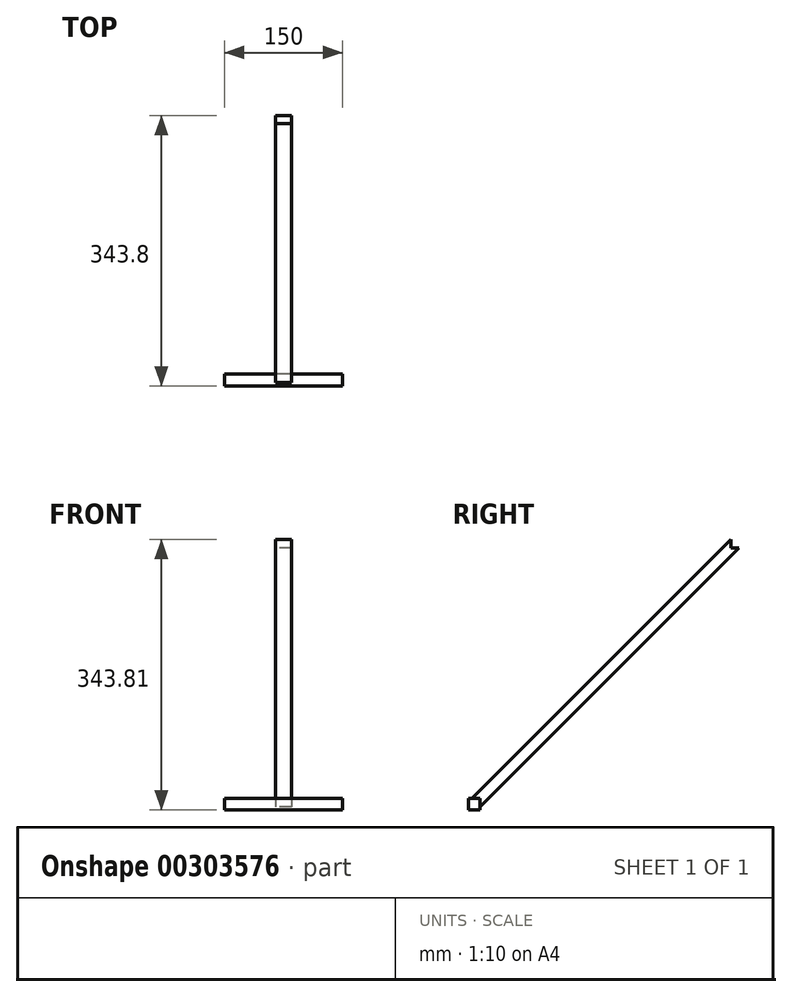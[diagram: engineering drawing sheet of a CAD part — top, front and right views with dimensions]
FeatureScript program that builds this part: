
annotation { "Feature Type Name" : "Feature", "Feature Type Description" : "" }
export const myFeature = defineFeature(function(context is Context, id is Id, definition is map)
    precondition{}
    {
        {
            var Q0;
            Q0=qCreatedBy(makeId("Right.planeOp"),FACE);
            var sketch = newSketch(context, id + "F0", { "sketchPlane" : qUnion([Q0])});
            skLineSegment(sketch, "E0", {"start": v(-179.3, -100.95) * mm, "end": v(149.5, 227.86) * mm});
            skLineSegment(sketch, "E1", {"start": v(160.1, 217.25) * mm, "end": v(-168.7, -111.55) * mm});
            skLineSegment(sketch, "E2", {"start": v(-168.7, -111.55) * mm, "end": v(-179.3, -100.95) * mm});
            skLineSegment(sketch, "E3", {"start": v(13.12, 43.85) * mm, "end": v(-59.7, -28.97) * mm, "construction": true});
            skLineSegment(sketch, "E4.bottom", {"start": v(160.1, 217.25) * mm, "end": v(149.5, 217.25) * mm});
            skLineSegment(sketch, "E4.right", {"start": v(149.5, 217.25) * mm, "end": v(149.5, 227.86) * mm});
            skPoint(sketch, "E4.middle", {"position": v(157.73, 225.48) * mm});
            skLineSegment(sketch, "E5.bottom", {"start": v(-183.7, -100.95) * mm, "end": v(-168.7, -100.95) * mm});
            skLineSegment(sketch, "E5.top", {"start": v(-183.7, -115.95) * mm, "end": v(-168.7, -115.95) * mm});
            skLineSegment(sketch, "E5.left", {"start": v(-183.7, -100.95) * mm, "end": v(-183.7, -115.95) * mm});
            skLineSegment(sketch, "E5.right", {"start": v(-168.7, -100.95) * mm, "end": v(-168.7, -115.95) * mm});
            skPoint(sketch, "E5.middle", {"position": v(-176.2, -108.45) * mm});
            skLineSegment(sketch, "E6", {"start": v(149.5, 227.86) * mm, "end": v(149.5, 217.25) * mm, "construction": true});
            skLineSegment(sketch, "E7", {"start": v(160.1, 217.25) * mm, "end": v(149.5, 217.25) * mm, "construction": true});
            skPoint(sketch, "E4.top.end.orphan", {"position": v(149.5, 233.72) * mm});
            skPoint(sketch, "E4.left.end.orphan", {"position": v(165.96, 233.72) * mm});
            skPoint(sketch, "E8.orphan", {"position": v(165.96, 217.25) * mm});
            skLineSegment(sketch, "E9.bottom", {"start": v(-179.3, -100.95) * mm, "end": v(-168.7, -100.95) * mm, "construction": true});
            skLineSegment(sketch, "E9.top", {"start": v(-179.3, -111.55) * mm, "end": v(-168.7, -111.55) * mm, "construction": true});
            skLineSegment(sketch, "E9.left", {"start": v(-179.3, -100.95) * mm, "end": v(-179.3, -111.55) * mm, "construction": true});
            skLineSegment(sketch, "E9.right", {"start": v(-168.7, -100.95) * mm, "end": v(-168.7, -111.55) * mm, "construction": true});
            skLineSegment(sketch, "E10", {"start": v(149.5, 227.86) * mm, "end": v(160.1, 227.86) * mm, "construction": true});
            skLineSegment(sketch, "E11", {"start": v(160.1, 217.25) * mm, "end": v(160.1, 227.86) * mm, "construction": true});
            skLineSegment(sketch, "E12", {"start": v(149.5, 233.72) * mm, "end": v(165.96, 233.72) * mm, "construction": true});
            skSolve(sketch);
        }
        {
            var Q0;
            {var subQ1=sQuery(id+"F0.wireOp",EDGE,"E0");Q0=makeQuery(id+"F0.imprint","IMPRINT",FACE,{"disambiguationData":[TD([[makeQuery(id+"F0.imprint","IMPRINT",EDGE,{"derivedFrom":subQ1}),-1.0]])]});}
            extrude(context, id + "F1", {"entities" : qUnion([Q0]), "endBound" : BoundingType.SYMMETRIC, "depth" : 20 * mm});
        }
        {
            var Q0;
            {var subQ2=sQuery(id+"F0.wireOp",EDGE,"E2");Q0=makeQuery(id+"F0.imprint","IMPRINT",FACE,{"disambiguationData":[TD([[makeQuery(id+"F0.imprint","IMPRINT",EDGE,{"derivedFrom":subQ2}),1.0]])]});}
            var Q1;
            {var subQ0=sQuery(id+"F0.wireOp",EDGE,"E2");Q1=makeQuery(id+"F0.imprint","IMPRINT",FACE,{"disambiguationData":[TD([[makeQuery(id+"F0.imprint","IMPRINT",EDGE,{"derivedFrom":subQ0}),-1.0]])]});}
            extrude(context, id + "F2", {"entities" : qUnion([Q0, Q1]), "operationType" : NewBodyOperationType.ADD, "endBound" : BoundingType.SYMMETRIC, "depth" : 150 * mm});
        }
    });
